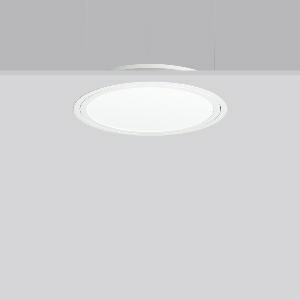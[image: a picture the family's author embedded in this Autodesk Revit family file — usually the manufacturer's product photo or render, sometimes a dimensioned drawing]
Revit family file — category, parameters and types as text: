
# Revit family: triona_round_e_312419_002_1_12_6d48
name_source: partatom
category: Lighting Fixtures
units: mm (PartAtom-declared; Revit-internal decimal feet)

## family parameters
Cut with Voids When Loaded = No
Host = Face
Light Source = No
Part Type = Normal
Room Calculation Point = No
Round Connector Dimension = Use Diameter
Shared = No

## types (1)
- TRIONA round E (1 x LED Modul 840, 4900 lm, 4000)
    Apparent Load = 48 VA
    CIE Flux Codes = 49 80 96 100 100
    Color Rendering = 80
    Color Temperature = 4000
    Default Elevation = 1800 mm
    Description = Series: TRIONA round
Decorative round LED recessed surface luminaire. Cover made of sheet steel, powder-coated. Frame made of aluminium, powder-coated. Recessed ring: aluminium extrusion profile, powder coated. Light emission through a diffuser: plastic, opal. Lightguide and diffuser made of non-yellowing plastic (PMMA). Lateral light emission (RZB SIDELITE technology) for above-average homogeneous light distribution. Suitable for installation in cavity ceilings. Tool-free mounting system thanks to the rocker arm mechanism (patent pending). Electronic ballast included. Very easy installation thanks to Plug+Play connection. 
Colour: traffic white, matt (RAL 9016)
Diameter: 505 mm
Height: 2 mm
Cut-out diameter: 482 mm
Recess height: 100 mm
Luminaire: recess height: 89 mm
Lamp: LED
Socket: without socket
Colour temperature: 4000K
Colour rendering index (CRI): 80
System power: 48 W
Rated luminous flux: 4900 lm
Luminous efficiency: 102 lm/W
Control gear: Converter, dimmable, DALI
Protection class: I
Type of protection: IP 40
    Height = 0 mm  [stored 0 ft]
    Lamp = 1 x LED Modul 840
    Lamp Light Flux = 4900 lm
    Lamp count = 1
    Length = 505 mm
    Lifetime = 50000 h
    Luminous efficacy = 102 lm/W
    Manufacturer = RZB
    ModVariant = No
    Model = 312419.002.1.12
    Mounting Place = Ceiling
    Mounting Type = Recessed
    Number of Poles = 1
    OnlyDefault = Yes
    Power Factor = 1
    Product Name = TRIONA round E
    Product group = Recessed modular luminaires
    ProductGroupID = 406
    Protection Class = Protection class I
    Protection Degree = IP 20
    RLX_Detail_Level = 1
    RLX_Emergency_Light_Flux = 0 lm
    RLX_Emergency_Type = 0
    RLX_Emergency_Type_DB = No
    RlxData = <blob elided: 30845 chars, md5=cd02eed0>
    Socket = socket
    Standby Power = 0 W
    System Light Flux = 4900 lm
    System Power = 48 W
    Type Comments = Product without accessories
    Type Image = 312419.002.12.jpg
    URL = http://relux.com
    VarID = ---
    Voltage = 230 V
    Voltage Range = 220-240 V
    Weight = 0.00 kg
    Width = 0 mm  [stored 0 ft]

note: [stored X ft] marks values corroborated as IEEE doubles in the binary element streams (Revit-internal decimal feet)

## geometry (parser evidence)
native form markers: Blend x4, Sweep x9
no freeform markers — native parametric forms only
